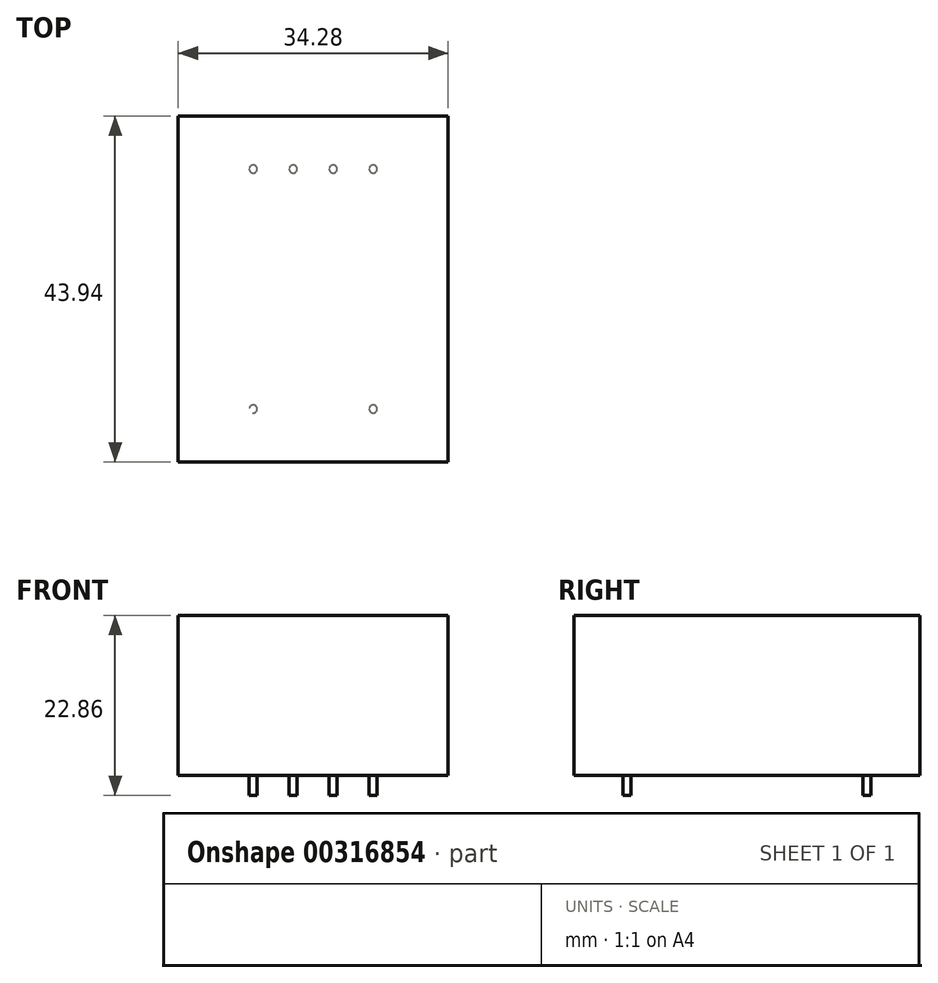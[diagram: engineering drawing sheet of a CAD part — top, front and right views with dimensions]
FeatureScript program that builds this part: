
annotation { "Feature Type Name" : "Feature", "Feature Type Description" : "" }
export const myFeature = defineFeature(function(context is Context, id is Id, definition is map)
    precondition{}
    {
        {
            var Q0;
            Q0=qCreatedBy(makeId("Top.planeOp"),FACE);
            var sketch = newSketch(context, id + "F0", { "sketchPlane" : qUnion([Q0])});
            skLineSegment(sketch, "E0.bottom", {"start": v(17.14, 21.97) * mm, "end": v(-17.15, 21.97) * mm});
            skLineSegment(sketch, "E0.top", {"start": v(17.15, -21.97) * mm, "end": v(-17.14, -21.97) * mm});
            skLineSegment(sketch, "E0.left", {"start": v(17.14, 21.97) * mm, "end": v(17.15, -21.97) * mm});
            skLineSegment(sketch, "E0.right", {"start": v(-17.15, 21.97) * mm, "end": v(-17.14, -21.97) * mm});
            skPoint(sketch, "E0.middle", {"position": v(0, 0) * mm});
            skSolve(sketch);
        }
        {
            var Q0;
            Q0=makeQuery(id+"F0.imprint","IMPRINT",FACE,{"disambiguationData":[TD([[makeQuery(id+"F0.imprint","IMPRINT",EDGE,{"derivedFrom":sQuery(id+"F0.wireOp",EDGE,"E0.bottom")}),1.0]])]});
            extrude(context, id + "F1", {"entities" : qUnion([Q0]), "depth" : 20.32 * mm});
        }
        {
            var Q0;
            Q0=makeQuery(id+"F1.opExtrude","CAP_FACE",FACE,{"disambiguationData":[OSD([sQuery(id+"F0.wireOp",EDGE,"E0.bottom"),sQuery(id+"F0.wireOp",EDGE,"E0.top"),sQuery(id+"F0.wireOp",EDGE,"E0.left"),sQuery(id+"F0.wireOp",EDGE,"E0.right")])],"isStart":true});
            var sketch = newSketch(context, id + "F2", { "sketchPlane" : qUnion([Q0])});
            skCircle(sketch, "E1", {"center": v(-7.62, 15.24) * mm, "radius": 0.5 * mm});
            skCircle(sketch, "E2", {"center": v(7.62, 15.24) * mm, "radius": 0.5 * mm});
            skCircle(sketch, "E3", {"center": v(-7.62, -15.24) * mm, "radius": 0.5 * mm});
            skCircle(sketch, "E4", {"center": v(7.62, -15.24) * mm, "radius": 0.5 * mm});
            skCircle(sketch, "E5", {"center": v(-2.54, -15.24) * mm, "radius": 0.5 * mm});
            skCircle(sketch, "E6", {"center": v(2.54, -15.24) * mm, "radius": 0.5 * mm});
            skSolve(sketch);
        }
        {
            var Q0;
            Q0=makeQuery(id+"F2.imprint","IMPRINT",FACE,{"disambiguationData":[TD([[makeQuery(id+"F2.imprint","IMPRINT",EDGE,{"derivedFrom":sQuery(id+"F2.wireOp",EDGE,"E1")}),1.0]])]});
            var Q1;
            Q1=makeQuery(id+"F2.imprint","IMPRINT",FACE,{"disambiguationData":[TD([[makeQuery(id+"F2.imprint","IMPRINT",EDGE,{"derivedFrom":sQuery(id+"F2.wireOp",EDGE,"E2")}),1.0]])]});
            var Q2;
            Q2=makeQuery(id+"F2.imprint","IMPRINT",FACE,{"disambiguationData":[TD([[makeQuery(id+"F2.imprint","IMPRINT",EDGE,{"derivedFrom":sQuery(id+"F2.wireOp",EDGE,"E3")}),1.0]])]});
            var Q3;
            Q3=makeQuery(id+"F2.imprint","IMPRINT",FACE,{"disambiguationData":[TD([[makeQuery(id+"F2.imprint","IMPRINT",EDGE,{"derivedFrom":sQuery(id+"F2.wireOp",EDGE,"E5")}),1.0]])]});
            var Q4;
            Q4=makeQuery(id+"F2.imprint","IMPRINT",FACE,{"disambiguationData":[TD([[makeQuery(id+"F2.imprint","IMPRINT",EDGE,{"derivedFrom":sQuery(id+"F2.wireOp",EDGE,"E6")}),1.0]])]});
            var Q5;
            Q5=makeQuery(id+"F2.imprint","IMPRINT",FACE,{"disambiguationData":[TD([[makeQuery(id+"F2.imprint","IMPRINT",EDGE,{"derivedFrom":sQuery(id+"F2.wireOp",EDGE,"E4")}),1.0]])]});
            extrude(context, id + "F3", {"entities" : qUnion([Q0, Q1, Q2, Q3, Q4, Q5]), "operationType" : NewBodyOperationType.ADD, "depth" : 2.54 * mm});
        }
    });
